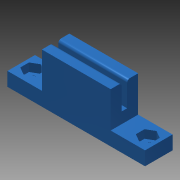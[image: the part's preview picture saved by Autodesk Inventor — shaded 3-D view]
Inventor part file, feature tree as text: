
AUTODESK INVENTOR PART (.ipt)
format: ipt  version: 2013 SP2 (Build 170200200, 200)  size: 136,192 bytes
history: native  units: mm
features: extrude x4, sketch x4, fillet x1
ambient origin geometry x8: Origin, YZ Plane, XZ Plane, XY Plane, X Axis, Y Axis, Z Axis, Center Point
bodies: Solid1 (feature_tree)
feature tree (9):
  extrude  "Extrusion1"  Depth=10.0mm
  extrude  "Extrusion2"  Depth=25.0mm
  fillet  "Fillet1"  Radius=25.0mm
  extrude  "Extrusion3"  Depth=3.0mm
  extrude  "Extrusion4"  Depth=4.0mm
  sketch  "Sketch1"  dims[d0=50.0mm d1=10.0mm]
  sketch  "Sketch2"  dims[d4=5.0mm d5=0.0mm d14=25.0mm d15=25.0mm]
  sketch  "Sketch3"  dims[d20=13.0mm d21=0.0mm d22=3.0mm]
  sketch  "Sketch4"  dims[d23=3.0mm d24=4.0mm d25=4.0mm d31=2.0mm d32=4.0mm d33=4.0mm d34=1.0mm d37=3.0mm d38=0.0mm d39=5.5mm d40=5.5mm d41=4.0mm d42=0.0mm]
